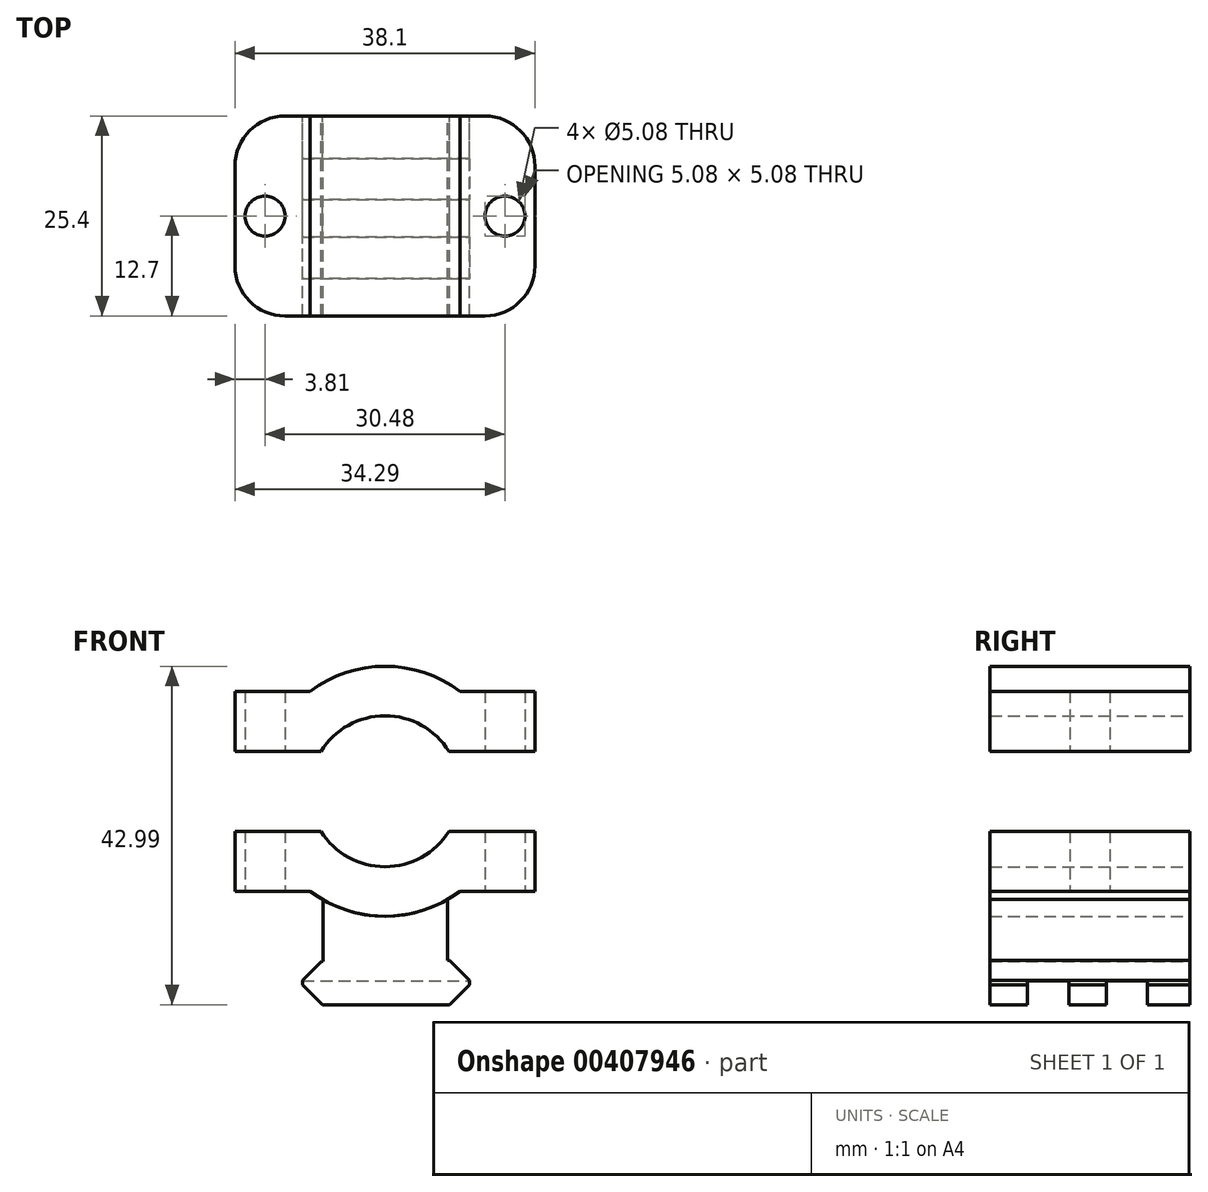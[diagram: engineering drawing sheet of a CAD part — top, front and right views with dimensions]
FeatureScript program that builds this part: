
annotation { "Feature Type Name" : "Feature", "Feature Type Description" : "" }
export const myFeature = defineFeature(function(context is Context, id is Id, definition is map)
    precondition{}
    {
        {
            var Q0;
            Q0=qCreatedBy(makeId("Front.planeOp"),FACE);
            var sketch = newSketch(context, id + "F0", { "sketchPlane" : qUnion([Q0])});
            skArc(sketch, "E0", {"start": v(-8.13, -5.08) * mm, "mid": v(0, -9.59) * mm, "end": v(8.13, -5.08) * mm});
            skArc(sketch, "E1", {"start": v(-9.52, -12.7) * mm, "mid": v(0, -15.88) * mm, "end": v(9.53, -12.7) * mm});
            skLineSegment(sketch, "E2.bottom", {"start": v(-19.05, 5.08) * mm, "end": v(-8.13, 5.08) * mm});
            skLineSegment(sketch, "E2.top", {"start": v(-19.05, -5.08) * mm, "end": v(-8.13, -5.08) * mm});
            skLineSegment(sketch, "E3.trimOffspring", {"start": v(8.13, 5.08) * mm, "end": v(19.05, 5.08) * mm});
            skLineSegment(sketch, "E4.trimOffspring", {"start": v(8.13, -5.08) * mm, "end": v(19.05, -5.08) * mm});
            skArc(sketch, "E5.trimOffspring", {"start": v(8.13, 5.08) * mm, "mid": v(0, 9.59) * mm, "end": v(-8.13, 5.08) * mm});
            skArc(sketch, "E6.trimOffspring", {"start": v(9.52, 12.7) * mm, "mid": v(0, 15.87) * mm, "end": v(-9.53, 12.7) * mm});
            skLineSegment(sketch, "E7", {"start": v(-19.05, -5.08) * mm, "end": v(-19.05, -12.7) * mm});
            skLineSegment(sketch, "E8", {"start": v(-19.05, -12.7) * mm, "end": v(-9.52, -12.7) * mm});
            skLineSegment(sketch, "E9", {"start": v(19.05, -5.08) * mm, "end": v(19.05, -12.7) * mm});
            skLineSegment(sketch, "E10", {"start": v(19.05, -12.7) * mm, "end": v(9.53, -12.7) * mm});
            skLineSegment(sketch, "E11", {"start": v(19.05, 5.08) * mm, "end": v(19.05, 12.7) * mm});
            skLineSegment(sketch, "E12", {"start": v(19.05, 12.7) * mm, "end": v(9.52, 12.7) * mm});
            skLineSegment(sketch, "E13", {"start": v(-19.05, 5.08) * mm, "end": v(-19.05, 12.7) * mm});
            skLineSegment(sketch, "E14", {"start": v(-19.05, 12.7) * mm, "end": v(-9.53, 12.7) * mm});
            skSolve(sketch);
        }
        {
            var Q0;
            Q0=makeQuery(id+"F0.imprint","IMPRINT",FACE,{"disambiguationData":[TD([[makeQuery(id+"F0.imprint","IMPRINT",EDGE,{"derivedFrom":sQuery(id+"F0.wireOp",EDGE,"E2.bottom")}),1.0]])]});
            var Q1;
            Q1=makeQuery(id+"F0.imprint","IMPRINT",FACE,{"disambiguationData":[TD([[makeQuery(id+"F0.imprint","IMPRINT",EDGE,{"derivedFrom":sQuery(id+"F0.wireOp",EDGE,"E0")}),-1.0]])]});
            extrude(context, id + "F1", {"entities" : qUnion([Q0, Q1]), "depth" : 25.4 * mm});
        }
        {
            var Q0;
            Q0=qCreatedBy(makeId("Front.planeOp"),FACE);
            var sketch = newSketch(context, id + "F2", { "sketchPlane" : qUnion([Q0])});
            skLineSegment(sketch, "E15", {"start": v(-7.84, -12.7) * mm, "end": v(7.98, -12.7) * mm});
            skLineSegment(sketch, "E16", {"start": v(7.98, -12.7) * mm, "end": v(7.98, -21.51) * mm});
            skLineSegment(sketch, "E17", {"start": v(7.98, -21.51) * mm, "end": v(8.2, -21.51) * mm});
            skLineSegment(sketch, "E18", {"start": v(8.2, -21.51) * mm, "end": v(10.74, -24.05) * mm});
            skLineSegment(sketch, "E19", {"start": v(10.74, -24.05) * mm, "end": v(10.74, -24.58) * mm});
            skLineSegment(sketch, "E20", {"start": v(10.74, -24.58) * mm, "end": v(8.2, -27.11) * mm});
            skLineSegment(sketch, "E21", {"start": v(8.2, -27.11) * mm, "end": v(-7.95, -27.11) * mm});
            skLineSegment(sketch, "E22", {"start": v(-7.95, -27.11) * mm, "end": v(-10.48, -24.58) * mm});
            skLineSegment(sketch, "E23", {"start": v(-10.48, -24.58) * mm, "end": v(-10.48, -24.05) * mm});
            skLineSegment(sketch, "E24", {"start": v(-10.48, -24.05) * mm, "end": v(-8.06, -21.63) * mm});
            skLineSegment(sketch, "E25", {"start": v(-8.06, -21.63) * mm, "end": v(-7.84, -21.63) * mm});
            skLineSegment(sketch, "E26", {"start": v(-7.84, -21.63) * mm, "end": v(-7.84, -12.7) * mm});
            skSolve(sketch);
        }
        {
            var Q0;
            Q0=makeQuery(id+"F2.imprint","IMPRINT",FACE,{"disambiguationData":[TD([[makeQuery(id+"F2.imprint","IMPRINT",EDGE,{"derivedFrom":sQuery(id+"F2.wireOp",EDGE,"E15")}),-1.0]])]});
            extrude(context, id + "F3", {"entities" : qUnion([Q0]), "depth" : 25.4 * mm});
        }
        {
            var Q0;
            Q0=qCreatedBy(makeId("Right.planeOp"),FACE);
            var sketch = newSketch(context, id + "F4", { "sketchPlane" : qUnion([Q0])});
            skLineSegment(sketch, "E27.bottom", {"start": v(-15.4, -24.11) * mm, "end": v(-20.62, -24.11) * mm});
            skLineSegment(sketch, "E27.top", {"start": v(-15.4, -40.12) * mm, "end": v(-20.62, -40.12) * mm});
            skLineSegment(sketch, "E27.left", {"start": v(-15.4, -24.11) * mm, "end": v(-15.4, -40.12) * mm});
            skLineSegment(sketch, "E27.right", {"start": v(-20.62, -24.11) * mm, "end": v(-20.62, -40.12) * mm});
            skLineSegment(sketch, "E28.bottom", {"start": v(-5.38, -24.11) * mm, "end": v(-10.62, -24.11) * mm});
            skLineSegment(sketch, "E28.top", {"start": v(-5.38, -42.9) * mm, "end": v(-10.62, -42.9) * mm});
            skLineSegment(sketch, "E28.left", {"start": v(-5.38, -24.11) * mm, "end": v(-5.38, -42.9) * mm});
            skLineSegment(sketch, "E28.right", {"start": v(-10.62, -24.11) * mm, "end": v(-10.62, -42.9) * mm});
            skSolve(sketch);
        }
        {
            var Q0;
            Q0=makeQuery(id+"F4.imprint","IMPRINT",FACE,{"disambiguationData":[TD([[makeQuery(id+"F4.imprint","IMPRINT",EDGE,{"derivedFrom":sQuery(id+"F4.wireOp",EDGE,"E28.bottom")}),1.0]])]});
            var Q1;
            Q1=makeQuery(id+"F4.imprint","IMPRINT",FACE,{"disambiguationData":[TD([[makeQuery(id+"F4.imprint","IMPRINT",EDGE,{"derivedFrom":sQuery(id+"F4.wireOp",EDGE,"E27.bottom")}),1.0]])]});
            extrude(context, id + "F5", {"entities" : qUnion([Q0, Q1]), "operationType" : NewBodyOperationType.REMOVE, "endBound" : BoundingType.SYMMETRIC, "oppositeDirection" : true, "depth" : 25.4 * mm});
        }
        {
            var Q0;
            Q0=makeQuery(id+"F1.opExtrude","SWEPT_BODY",BODY,{"disambiguationData":[OSD([sQuery(id+"F0.wireOp",EDGE,"E0"),sQuery(id+"F0.wireOp",EDGE,"E1"),sQuery(id+"F0.wireOp",EDGE,"E2.top"),sQuery(id+"F0.wireOp",EDGE,"E4.trimOffspring"),sQuery(id+"F0.wireOp",EDGE,"E7"),sQuery(id+"F0.wireOp",EDGE,"E8"),sQuery(id+"F0.wireOp",EDGE,"E9"),sQuery(id+"F0.wireOp",EDGE,"E10")])]});
            var Q1;
            Q1=makeQuery(id+"F3.opExtrude","SWEPT_BODY",BODY,{"disambiguationData":[OSD([sQuery(id+"F2.wireOp",EDGE,"E15"),sQuery(id+"F2.wireOp",EDGE,"E16"),sQuery(id+"F2.wireOp",EDGE,"E17"),sQuery(id+"F2.wireOp",EDGE,"E18"),sQuery(id+"F2.wireOp",EDGE,"E19"),sQuery(id+"F2.wireOp",EDGE,"E20"),sQuery(id+"F2.wireOp",EDGE,"E21"),sQuery(id+"F2.wireOp",EDGE,"E22"),sQuery(id+"F2.wireOp",EDGE,"E23"),sQuery(id+"F2.wireOp",EDGE,"E24"),sQuery(id+"F2.wireOp",EDGE,"E25"),sQuery(id+"F2.wireOp",EDGE,"E26")])]});
            booleanBodies(context, id + "F6", {"operationType" : BooleanOperationType.SUBTRACTION, "tools" : qUnion([Q0]), "targets" : qUnion([Q1]), "keepTools" : true});
        }
        {
            var Q0;
            Q0=makeQuery(id+"F1.opExtrude","CAP_EDGE",EDGE,{"disambiguationData":[OSD([sQuery(id+"F0.wireOp",EDGE,"E7")])],"isStart":true});
            var Q1;
            Q1=makeQuery(id+"F1.opExtrude","CAP_EDGE",EDGE,{"disambiguationData":[OSD([sQuery(id+"F0.wireOp",EDGE,"E13")])],"isStart":true});
            var Q2;
            Q2=makeQuery(id+"F1.opExtrude","CAP_EDGE",EDGE,{"disambiguationData":[OSD([sQuery(id+"F0.wireOp",EDGE,"E13")])],"isStart":false});
            var Q3;
            Q3=makeQuery(id+"F1.opExtrude","CAP_EDGE",EDGE,{"disambiguationData":[OSD([sQuery(id+"F0.wireOp",EDGE,"E7")])],"isStart":false});
            var Q4;
            Q4=makeQuery(id+"F1.opExtrude","CAP_EDGE",EDGE,{"disambiguationData":[OSD([sQuery(id+"F0.wireOp",EDGE,"E9")])],"isStart":false});
            var Q5;
            Q5=makeQuery(id+"F1.opExtrude","CAP_EDGE",EDGE,{"disambiguationData":[OSD([sQuery(id+"F0.wireOp",EDGE,"E11")])],"isStart":false});
            var Q6;
            Q6=makeQuery(id+"F1.opExtrude","CAP_EDGE",EDGE,{"disambiguationData":[OSD([sQuery(id+"F0.wireOp",EDGE,"E9")])],"isStart":true});
            var Q7;
            Q7=makeQuery(id+"F1.opExtrude","CAP_EDGE",EDGE,{"disambiguationData":[OSD([sQuery(id+"F0.wireOp",EDGE,"E11")])],"isStart":true});
            fillet(context, id + "F7", {"entities" : qUnion([Q0, Q1, Q2, Q3, Q4, Q5, Q6, Q7]), "radius" : 6.35 * mm, "tangentPropagation" : true, "allowEdgeOverflow" : false});
        }
        {
            var Q0;
            Q0=makeQuery(id+"F1.opExtrude","SWEPT_FACE",FACE,{"disambiguationData":[OSD([sQuery(id+"F0.wireOp",EDGE,"E10")])]});
            var sketch = newSketch(context, id + "F8", { "sketchPlane" : qUnion([Q0])});
            skCircle(sketch, "E29", {"center": v(-15.24, 12.7) * mm, "radius": 2.54 * mm});
            skCircle(sketch, "E30", {"center": v(15.24, 12.7) * mm, "radius": 2.54 * mm});
            skSolve(sketch);
        }
        {
            var Q0;
            Q0=makeQuery(id+"F8.imprint","IMPRINT",FACE,{"disambiguationData":[TD([[makeQuery(id+"F8.imprint","IMPRINT",EDGE,{"derivedFrom":sQuery(id+"F8.wireOp",EDGE,"E29")}),1.0]])]});
            var Q1;
            Q1=makeQuery(id+"F8.imprint","IMPRINT",FACE,{"disambiguationData":[TD([[makeQuery(id+"F8.imprint","IMPRINT",EDGE,{"derivedFrom":sQuery(id+"F8.wireOp",EDGE,"E30")}),1.0]])]});
            extrude(context, id + "F9", {"entities" : qUnion([Q0, Q1]), "operationType" : NewBodyOperationType.REMOVE, "oppositeDirection" : true, "depth" : 38.1 * mm});
        }
    });
